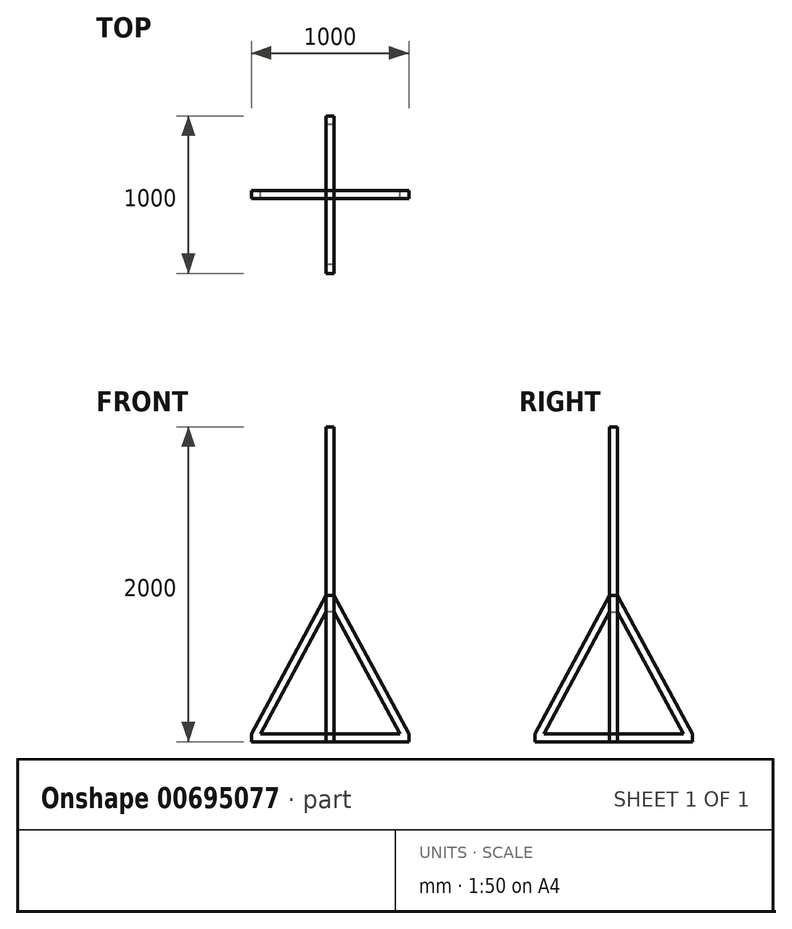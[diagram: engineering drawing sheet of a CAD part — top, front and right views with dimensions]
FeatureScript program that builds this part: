
annotation { "Feature Type Name" : "Feature", "Feature Type Description" : "" }
export const myFeature = defineFeature(function(context is Context, id is Id, definition is map)
    precondition{}
    {
        {
            var Q0;
            Q0=qCreatedBy(makeId("Front.planeOp"),FACE);
            var sketch = newSketch(context, id + "F0", { "sketchPlane" : qUnion([Q0])});
            skLineSegment(sketch, "E0.bottom", {"start": v(0, 0) * mm, "end": v(50, 0) * mm});
            skLineSegment(sketch, "E0.top", {"start": v(0, 1000) * mm, "end": v(50, 1000) * mm});
            skLineSegment(sketch, "E0.left", {"start": v(0, 50) * mm, "end": v(0, 824.72) * mm});
            skLineSegment(sketch, "E0.right", {"start": v(50, 50) * mm, "end": v(50, 824.72) * mm});
            skLineSegment(sketch, "E1.bottom", {"start": v(-475, 0) * mm, "end": v(525, 0) * mm});
            skLineSegment(sketch, "E1.top", {"start": v(-418.18, 50) * mm, "end": v(0, 50) * mm});
            skLineSegment(sketch, "E1.left", {"start": v(-475, 0) * mm, "end": v(-475, 50) * mm});
            skLineSegment(sketch, "E1.right", {"start": v(525, 0) * mm, "end": v(525, 50) * mm});
            skLineSegment(sketch, "E2", {"start": v(-475, 50) * mm, "end": v(0, 929.99) * mm});
            skLineSegment(sketch, "E3", {"start": v(525, 50) * mm, "end": v(50, 929.99) * mm});
            skLineSegment(sketch, "E4", {"start": v(-418.18, 50) * mm, "end": v(0, 824.72) * mm});
            skLineSegment(sketch, "E5", {"start": v(50, 824.72) * mm, "end": v(468.18, 50) * mm});
            skLineSegment(sketch, "E6.trimOffspring", {"start": v(50, 50) * mm, "end": v(468.18, 50) * mm});
            skLineSegment(sketch, "E7.trimOffspring", {"start": v(0, 929.99) * mm, "end": v(0, 1000) * mm});
            skLineSegment(sketch, "E8.trimOffspring", {"start": v(50, 929.99) * mm, "end": v(50, 1000) * mm});
            skSolve(sketch);
        }
        {
            var Q0;
            Q0=qSketchRegion(id+"F0",true);
            extrude(context, id + "F1", {"entities" : qUnion([Q0]), "endBound" : BoundingType.SYMMETRIC, "depth" : 50 * mm, "offsetDistance" : 25 * mm});
        }
        {
            var Q0;
            Q0=qCreatedBy(makeId("Right.planeOp"),FACE);
            var sketch = newSketch(context, id + "F2", { "sketchPlane" : qUnion([Q0])});
            skLineSegment(sketch, "E9.bottom", {"start": v(-500, 0) * mm, "end": v(500, 0) * mm});
            skLineSegment(sketch, "E9.top", {"start": v(-443.18, 50) * mm, "end": v(-25, 50) * mm});
            skLineSegment(sketch, "E9.left", {"start": v(-500, 0) * mm, "end": v(-500, 50) * mm});
            skLineSegment(sketch, "E9.right", {"start": v(500, 0) * mm, "end": v(500, 50) * mm});
            skLineSegment(sketch, "E10.0", {"start": v(-25, 929.99) * mm, "end": v(25, 929.99) * mm});
            skLineSegment(sketch, "E11", {"start": v(-500, 50) * mm, "end": v(-25, 929.99) * mm});
            skLineSegment(sketch, "E12", {"start": v(500, 50) * mm, "end": v(25, 929.99) * mm});
            skPoint(sketch, "E13.0", {"position": v(-25, 824.72) * mm});
            skPoint(sketch, "E14.0", {"position": v(25, 824.72) * mm});
            skLineSegment(sketch, "E15", {"start": v(-25, 824.72) * mm, "end": v(-443.18, 50) * mm});
            skLineSegment(sketch, "E16", {"start": v(25, 824.72) * mm, "end": v(443.18, 50) * mm});
            skLineSegment(sketch, "E17", {"start": v(-25, 824.72) * mm, "end": v(-25, 50) * mm});
            skPoint(sketch, "E17.endSnap0", {"position": v(0, 50) * mm});
            skLineSegment(sketch, "E18", {"start": v(25, 824.72) * mm, "end": v(25, 50) * mm});
            skLineSegment(sketch, "E19.trimOffspring", {"start": v(25, 50) * mm, "end": v(443.18, 50) * mm});
            skSolve(sketch);
        }
        {
            var Q0;
            Q0=makeQuery(id+"F2.imprint","IMPRINT",FACE,{"disambiguationData":[TD([[makeQuery(id+"F2.imprint","IMPRINT",EDGE,{"derivedFrom":sQuery(id+"F2.wireOp",EDGE,"E9.bottom")}),1.0]])]});
            extrude(context, id + "F3", {"entities" : qUnion([Q0]), "operationType" : NewBodyOperationType.ADD, "depth" : 50 * mm, "offsetDistance" : 25 * mm});
        }
        {
            var Q0;
            Q0=makeQuery(id+"F1.opExtrude","SWEPT_FACE",FACE,{"disambiguationData":[OSD([sQuery(id+"F0.wireOp",EDGE,"E0.top")])]});
            extrude(context, id + "F4", {"entities" : qUnion([Q0]), "operationType" : NewBodyOperationType.ADD, "depth" : 1000 * mm, "offsetDistance" : 25 * mm});
        }
    });
